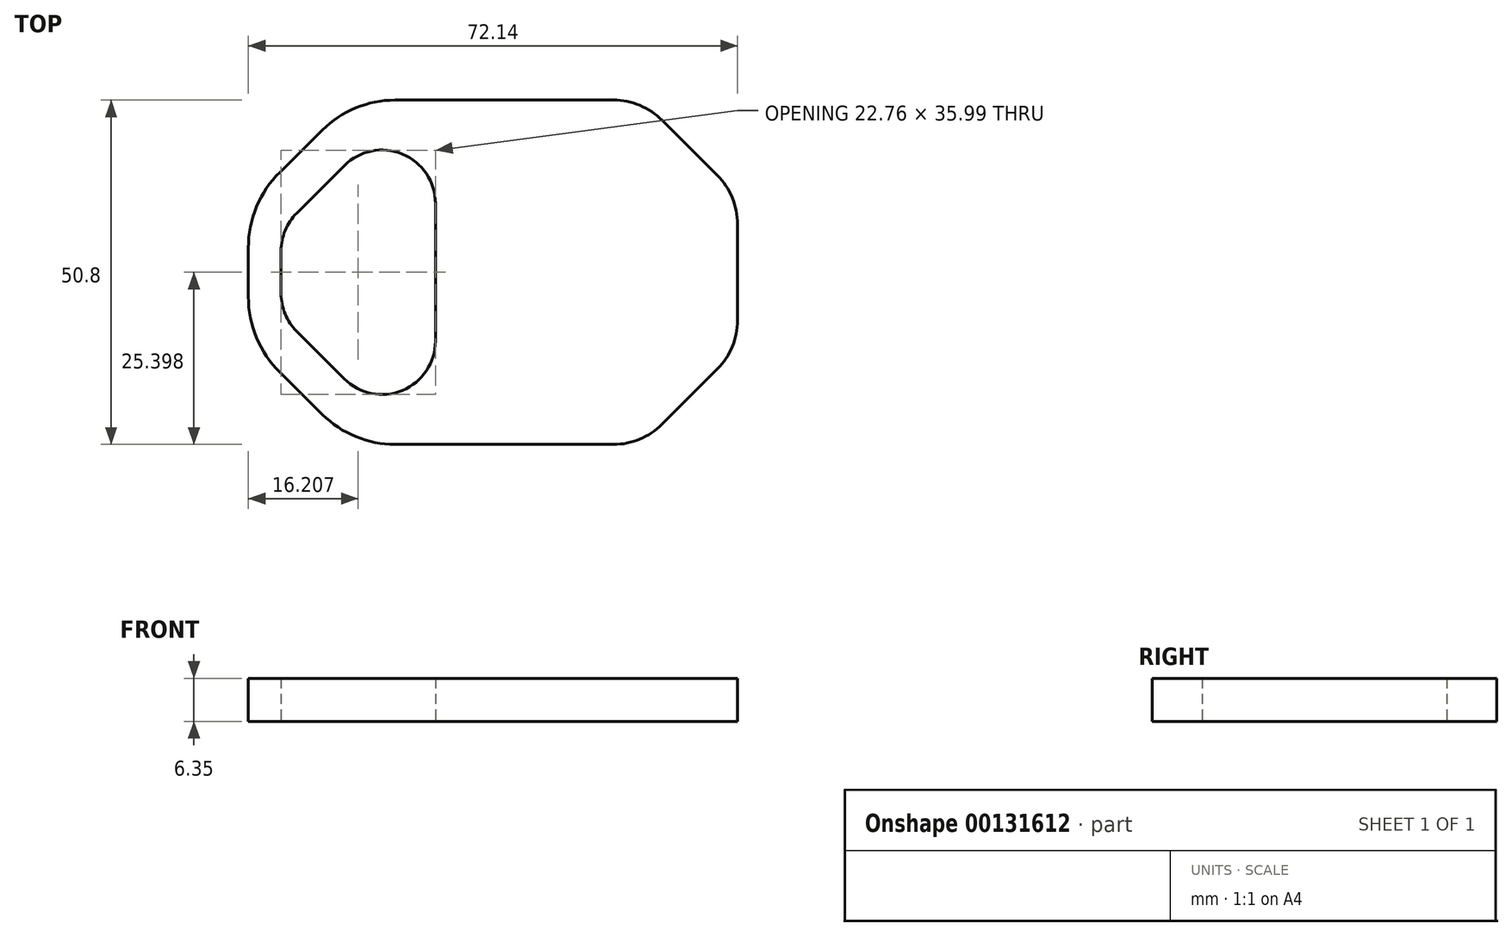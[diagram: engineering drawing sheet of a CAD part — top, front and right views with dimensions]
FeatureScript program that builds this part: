
annotation { "Feature Type Name" : "Feature", "Feature Type Description" : "" }
export const myFeature = defineFeature(function(context is Context, id is Id, definition is map)
    precondition{}
    {
        {
            var Q0;
            Q0=qCreatedBy(makeId("Top.planeOp"),FACE);
            var sketch = newSketch(context, id + "F0", { "sketchPlane" : qUnion([Q0])});
            skPoint(sketch, "E0", {"position": v(72.4, -36.91) * mm});
            skPoint(sketch, "E1", {"position": v(58.31, -51.01) * mm});
            skPoint(sketch, "E2.orphan", {"position": v(72.4, -51.01) * mm});
            skLineSegment(sketch, "E3.bottom", {"start": v(72.4, -32.7) * mm, "end": v(72.4, -18.52) * mm});
            skLineSegment(sketch, "E3.top", {"start": v(0.27, -29.21) * mm, "end": v(0.27, -22.01) * mm});
            skLineSegment(sketch, "E3.left", {"start": v(54.1, -51.01) * mm, "end": v(21.91, -51.01) * mm});
            skLineSegment(sketch, "E3.right", {"start": v(54.1, -0.21) * mm, "end": v(21.91, -0.21) * mm});
            skLineSegment(sketch, "E4", {"start": v(61.29, -48.04) * mm, "end": v(69.43, -39.9) * mm});
            skArc(sketch, "E5.filletArc", {"start": v(54.1, -51.01) * mm, "mid": v(58, -50.24) * mm, "end": v(61.29, -48.04) * mm});
            skArc(sketch, "E6.filletArc", {"start": v(69.43, -39.9) * mm, "mid": v(71.63, -36.6) * mm, "end": v(72.4, -32.7) * mm});
            skArc(sketch, "E7.MirrorCS", {"start": v(54.1, -0.21) * mm, "mid": v(58, -0.98) * mm, "end": v(61.29, -3.19) * mm});
            skLineSegment(sketch, "E8.MirrorCS", {"start": v(61.29, -3.19) * mm, "end": v(69.43, -11.33) * mm});
            skArc(sketch, "E9.MirrorCS", {"start": v(69.43, -11.33) * mm, "mid": v(71.63, -14.63) * mm, "end": v(72.4, -18.52) * mm});
            skPoint(sketch, "E10", {"position": v(15.64, -51.01) * mm});
            skPoint(sketch, "E11.MirrorP", {"position": v(15.64, -0.21) * mm});
            skPoint(sketch, "E12", {"position": v(0.27, -35.77) * mm});
            skLineSegment(sketch, "E13", {"start": v(11.18, -46.6) * mm, "end": v(4.93, -40.4) * mm});
            skArc(sketch, "E14.filletArc", {"start": v(11.18, -46.6) * mm, "mid": v(16.11, -49.86) * mm, "end": v(21.91, -51.01) * mm});
            skArc(sketch, "E15.filletArc", {"start": v(0.27, -29.21) * mm, "mid": v(1.48, -35.27) * mm, "end": v(4.93, -40.4) * mm});
            skArc(sketch, "E16.MirrorCS", {"start": v(11.18, -4.63) * mm, "mid": v(16.11, -1.36) * mm, "end": v(21.91, -0.21) * mm});
            skLineSegment(sketch, "E17.MirrorCS", {"start": v(11.18, -4.63) * mm, "end": v(4.93, -10.83) * mm});
            skArc(sketch, "E18.MirrorCS", {"start": v(0.27, -22.01) * mm, "mid": v(1.48, -15.96) * mm, "end": v(4.93, -10.83) * mm});
            skLineSegment(sketch, "E19", {"start": v(19.98, -35.77) * mm, "end": v(27.86, -35.77) * mm});
            skLineSegment(sketch, "E20", {"start": v(27.86, -35.77) * mm, "end": v(27.86, -15.45) * mm});
            skLineSegment(sketch, "E21", {"start": v(5.1, -28.76) * mm, "end": v(5.1, -22.46) * mm});
            skLineSegment(sketch, "E22", {"start": v(19.98, -35.77) * mm, "end": v(19.98, -43.65) * mm});
            skLineSegment(sketch, "E23", {"start": v(14.41, -41.34) * mm, "end": v(7.4, -34.33) * mm});
            skLineSegment(sketch, "E24.MirrorCS", {"start": v(14.41, -9.88) * mm, "end": v(7.4, -16.9) * mm});
            skArc(sketch, "E25.trimOffspring", {"start": v(14.41, -41.34) * mm, "mid": v(23, -43.05) * mm, "end": v(27.86, -35.77) * mm});
            skArc(sketch, "E26.trimOffspring", {"start": v(5.1, -22.46) * mm, "mid": v(5.7, -19.45) * mm, "end": v(7.4, -16.9) * mm});
            skArc(sketch, "E27.trimOffspring", {"start": v(5.1, -28.76) * mm, "mid": v(5.7, -31.77) * mm, "end": v(7.4, -34.33) * mm});
            skArc(sketch, "E28.trimOffspring", {"start": v(14.41, -9.88) * mm, "mid": v(23, -8.18) * mm, "end": v(27.86, -15.45) * mm});
            skPoint(sketch, "E29.trimOffspring.end.orphan", {"position": v(74.5, -25.61) * mm});
            skPoint(sketch, "E30.start.orphan", {"position": v(-2.05, -25.61) * mm});
            skSolve(sketch);
        }
        {
            var Q0;
            Q0=makeQuery(id+"F0.imprint","IMPRINT",FACE,{"disambiguationData":[TD([[makeQuery(id+"F0.imprint","IMPRINT",EDGE,{"derivedFrom":sQuery(id+"F0.wireOp",EDGE,"XA15pcHP-KK0X-gA3X-Lx07-giM8paJdqfh7")}),-1.0]])]});
            var Q1;
            Q1=makeQuery(id+"F0.imprint","IMPRINT",FACE,{"disambiguationData":[TD([[makeQuery(id+"F0.imprint","IMPRINT",EDGE,{"derivedFrom":sQuery(id+"F0.wireOp",EDGE,"E3.bottom")}),1.0]])]});
            extrude(context, id + "F1", {"entities" : qUnion([Q0, Q1]), "depth" : 6.35 * mm});
        }
    });
